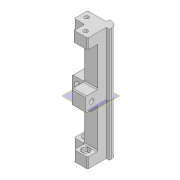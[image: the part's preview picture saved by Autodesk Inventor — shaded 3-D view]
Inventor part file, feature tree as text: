
AUTODESK INVENTOR PART (.ipt)
format: ipt  version: 2020 (Build 240168000, 168)  size: 328,192 bytes
history: native  units: mm
features: extrude x12, sketch x12, other x6, fillet x2
ambient origin geometry x8: Origin, YZ Plane, XZ Plane, XY Plane, X Axis, Y Axis, Z Axis, Center Point
bodies: Body1 (feature_tree)
feature tree (32):
  other  "Sólido1"
  extrude  "Extrusão1"  Depth=16.0mm
  extrude  "Extrusão2"  Depth=3.0mm
  extrude  "Extrusão3"  Depth=3.0mm
  extrude  "Extrusão4"  Depth=5.2mm
  extrude  "Extrusão5"  Depth=8.0mm
  fillet  "Arredondamento1"  Radius=110.0mm
  extrude  "Extrusão6"  Depth=10.0mm
  extrude  "Extrusão7"  TaperAngle=0.0deg  [1 undecoded]
  other  "Plano de trabalho1"
  extrude  "Extrusão9"  Depth=5.0mm
  extrude  "Extrusão10"  Depth=10.0mm
  extrude  "Extrusão11"  Depth=4.0mm
  extrude  "Extrusão12"  Depth=5.0mm
  extrude  "Extrusão13"  Depth=1.0mm TaperAngle=0.0deg
  fillet  "Arredondamento2"  Radius=1.0mm
  sketch  "Esboço1"  dims[d0=16.0mm d1=16.0mm]
  sketch  "Esboço2"  dims[d2=8.0mm d3=3.0mm]
  sketch  "Esboço3"  dims[d4=8.0mm d5=3.0mm]
  sketch  "Esboço4"  dims[d6=6.0mm d7=5.2mm]
  sketch  "Esboço5"  dims[d8=8.0mm d9=8.0mm d10=110.0mm d11=0.0mm]
  sketch  "Esboço6"  dims[d12=10.0mm d13=10.0mm]
  sketch  "Esboço7"  dims[d14=10.0mm d15=0.0mm d16=0.0mm]
  other  "Contorno projetado1"
  other  "Contorno projetado2"
  sketch  "Esboço9"  dims[d17=4.0mm d18=5.0mm]
  other  "Contorno projetado3"
  other  "Contorno projetado4"
  sketch  "Esboço10"  dims[d19=200.0mm d20=0.0mm d21=10.0mm]
  sketch  "Esboço11"  dims[d22=10.0mm d23=0.0mm d24=4.0mm]
  sketch  "Esboço12"  dims[d25=5.0mm d26=7.0mm]
  sketch  "Esboço13"  dims[d27=6.0mm d28=200.0mm d29=0.0mm d30=1.0mm d31=13.0mm d32=6.95mm d33=6.95mm d34=4.0mm d35=0.0mm d36=4.0mm d37=0.0mm d38=0.0mm d44=0.0mm d45=-50.0mm d46=12.0mm d47=12.0mm d48=2.0mm d49=0.0mm d50=12.0mm d51=0.0mm d52=4.5mm d53=6.0mm d54=20.0mm d55=0.0mm d56=4.5mm d57=6.0mm d58=20.0mm d59=0.0mm d60=6.95mm d61=4.0mm d62=0.0mm d63=6.95mm d64=4.0mm d65=0.0mm d66=1.0mm]
note: 1 required parameter value undecoded (feature->parameter linkage not recoverable at this tier; creation-order binding heuristic only, values carry confidence <= 0.55)
